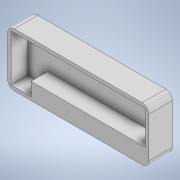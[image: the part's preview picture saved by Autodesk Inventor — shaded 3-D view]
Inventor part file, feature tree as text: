
AUTODESK INVENTOR PART (.ipt)
format: ipt  version: 2021 (Build 250183000, 183)  size: 122,880 bytes
history: native  units: mm
features: extrude x2, sketch x2, fillet x1, projected_geometry x1
ambient origin geometry x8: Origin, YZ Plane, XZ Plane, XY Plane, X Axis, Y Axis, Z Axis, Center Point
bodies: Solid1 (feature_tree)
feature tree (6):
  extrude  "Extrusion1"  Depth=42.0mm
  extrude  "Extrusion3"  Depth=40.0mm
  fillet  "Fillet2"  Radius=10.0mm
  sketch  "Sketch1"  dims[d6=2.0mm d7=0.0mm d11=42.0mm]
  sketch  "Sketch2"  dims[d12=16.0mm d13=40.0mm d14=10.0mm d15=6.0mm d16=4.0mm d17=5.0mm d18=0.0mm d19=2.0mm]
  projected_geometry  "Projected Loop1"
